# Revit family: Speaker-NearField-Panasonic-Ceiling_Mounted_RAMSA_WS-AR080SeriesX
name_source: partatom
category: Communication Devices
units: mm (PartAtom-declared; Revit-internal decimal feet)

## family parameters
Cut with Voids When Loaded = No
Host = Face
Maintain Annotation Orientation = Yes
OmniClass Number = 23.85.10.11.14.14.14
OmniClass Title = Loudspeakers
Part Type = Normal
Room Calculation Point = No
Round Connector Dimension = Use Diameter
Shared = No

## types (2) — shared parameters
Coverage = 60° x 60°
Date Last Modified = 2024/08/05
Default Elevation = 2700 mm  [stored 8.85827 ft]
Depth = 260 mm  [stored 0.853018 ft]
Equipment Abbreviation = SP
Family Version = 1.0.0
Frequency characteristic = 40 Hz～20 kHz（－20 dB、Typical、半自由空間）, 70 Hz～18 kHz（－10 dB、Typical、半自由空間）
Height = 455 mm
Input Impedance = 8 Ω
Input connector = 2個（パラレル、推奨プラグ NL2FX / NL4FX）
Manufacturer = Panasonic
Model Disclaimer = Contact Panasonic for more information
Operational Temperature = -10℃~+50℃
Pan Angle Max = 60.00°
Pan Angle Min = -60.00°
Pan Handle Length = 100 mm  [stored 0.328084 ft]
Product Documentation Link = https://partner.connect.panasonic.com
Product Page URL = https://connect.panasonic.com
Provide Feedback = https://connect.panasonic.com
Rated Input = 130W
SPL = 93 dB （1 W/m、Typical、半自由空間）
SV Visible = No
Sound Coverage Horizontal Angle = 60.00°
Sound Coverage Vertical Angle = 60.00°
Sound Power Level = 93
Speaker unit = 低域用 ：20 cmコーンスピーカー, 高域用 ：チタン振動板ドームツィーター（SCWGホーン）
Tilt Angle Min = 0.00°
Type = 2ウェイバスレフ形
URL = https://connect.panasonic.com
View Volume Material = Panasonic - ViewVolume
Weight = 10.00 kgf
Width = 312 mm  [stored 1.02362 ft]

## per-type parameters (varying)
| type | Description | Finish | Model | Part Description | Part Number | Product Material |
| RAMSA, WS-AR080W | RAMSA 20cm 2ウェイスピーカー WS-AR080-W | エンクロージャー ：PP樹脂成型、白色半艶塗装（マンセルN9近似色）, パンチングネット ：金属製（SPCC）、白色半艶塗装（マンセルN9近似色） | RAMSA 20cm 2ウェイスピーカー WS-AR080-W | RAMSA 20cm 2ウェイスピーカー WS-AR080-W | WS-AR080-W | Plastic - HIPS White (Munsell N9.3 Approx color） |
| RAMSA, WS-AR080K | RAMSA 20cm 2ウェイスピーカー WS-AR080-K | エンクロージャー ：PP樹脂成型、黒色半艶塗装（マンセルN1近似色） パンチングネット ：金属製（SPCC）、黒色半艶塗装（マンセルN1近似色） | RAMSA 20cm 2ウェイスピーカー WS-AR080-K | RAMSA 20cm 2ウェイスピーカー WS-AR080-K | WS-AR080-K | Plastic - HIPS Black (Munsell N1 Approx color) |

note: [stored X ft] marks values corroborated as IEEE doubles in the binary element streams (Revit-internal decimal feet)

## geometry (parser evidence)
native form markers: Blend x2, Sweep x5
no freeform markers — native parametric forms only
